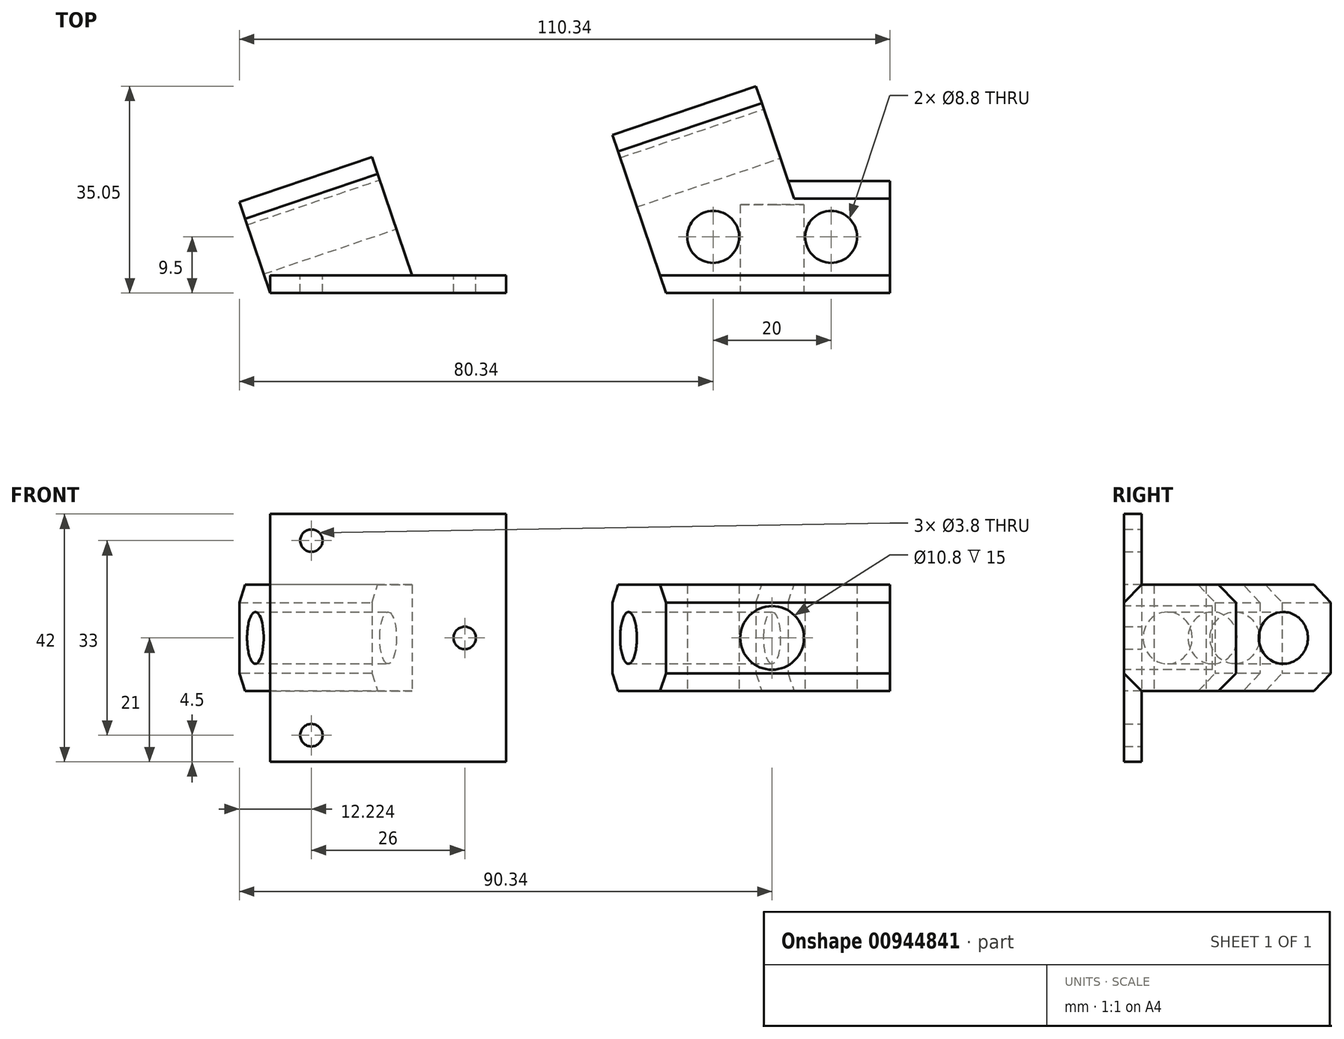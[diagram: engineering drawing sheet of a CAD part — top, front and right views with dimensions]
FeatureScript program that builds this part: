
annotation { "Feature Type Name" : "Feature", "Feature Type Description" : "" }
export const myFeature = defineFeature(function(context is Context, id is Id, definition is map)
    precondition{}
    {
        {
            var Q0;
            Q0=qCreatedBy(makeId("Top.planeOp"),FACE);
            var sketch = newSketch(context, id + "F0", { "sketchPlane" : qUnion([Q0])});
            skLineSegment(sketch, "E0.bottom", {"start": v(0, 0) * mm, "end": v(38, 0) * mm});
            skLineSegment(sketch, "E0.top", {"start": v(20.7, 19) * mm, "end": v(38, 19) * mm});
            skLineSegment(sketch, "E0.left", {"start": v(0, 0) * mm, "end": v(0, 19) * mm, "construction": true});
            skLineSegment(sketch, "E0.right", {"start": v(38, 0) * mm, "end": v(38, 19) * mm});
            skCircle(sketch, "E1", {"center": v(28, 9.5) * mm, "radius": 4.4 * mm});
            skPoint(sketch, "E1.centerSnap0", {"position": v(38, 9.5) * mm});
            skCircle(sketch, "E2", {"center": v(8, 9.5) * mm, "radius": 4.4 * mm});
            skLineSegment(sketch, "E3", {"start": v(8, 9.5) * mm, "end": v(28, 9.5) * mm, "construction": true});
            skLineSegment(sketch, "E4", {"start": v(18, 9.5) * mm, "end": v(18, 27) * mm, "construction": true});
            skLineSegment(sketch, "E5", {"start": v(18, 27) * mm, "end": v(-19.64, 14.26) * mm, "construction": true});
            skLineSegment(sketch, "E6", {"start": v(15.27, 35.05) * mm, "end": v(20.7, 19) * mm});
            skLineSegment(sketch, "E7", {"start": v(15.27, 35.05) * mm, "end": v(-9.07, 26.8) * mm});
            skLineSegment(sketch, "E8", {"start": v(0, 0) * mm, "end": v(-9.07, 26.8) * mm});
            skLineSegment(sketch, "E9", {"start": v(-67.12, 0) * mm, "end": v(-27.12, 0) * mm});
            skLineSegment(sketch, "E10", {"start": v(-27.12, 0) * mm, "end": v(-27.12, 3) * mm});
            skLineSegment(sketch, "E11", {"start": v(-27.12, 3) * mm, "end": v(-67.12, 3) * mm});
            skLineSegment(sketch, "E12", {"start": v(-67.12, 3) * mm, "end": v(-67.12, 0) * mm});
            skLineSegment(sketch, "E13", {"start": v(-47.12, 0) * mm, "end": v(-47.12, 15) * mm, "construction": true});
            skPoint(sketch, "E13.endSnap0", {"position": v(-47.12, 3) * mm});
            skLineSegment(sketch, "E14", {"start": v(-47.12, 15) * mm, "end": v(-73.5, 6.07) * mm, "construction": true});
            skLineSegment(sketch, "E15", {"start": v(-49.84, 23.05) * mm, "end": v(-43.05, 3) * mm});
            skLineSegment(sketch, "E16", {"start": v(-49.84, 23.05) * mm, "end": v(-72.34, 15.44) * mm});
            skLineSegment(sketch, "E17", {"start": v(-72.34, 15.44) * mm, "end": v(-67.12, 0) * mm});
            skSolve(sketch);
        }
        {
            var Q0;
            Q0=makeQuery(id+"F0.imprint","IMPRINT",FACE,{"disambiguationData":[TD([[makeQuery(id+"F0.imprint","IMPRINT",EDGE,{"derivedFrom":sQuery(id+"F0.wireOp",EDGE,"E0.bottom")}),1.0]])]});
            extrude(context, id + "F1", {"entities" : qUnion([Q0]), "depth" : 18 * mm, "offsetDistance" : 25 * mm});
        }
        {
            var Q0;
            Q0=qCreatedBy(makeId("Front.planeOp"),FACE);
            var sketch = newSketch(context, id + "F2", { "sketchPlane" : qUnion([Q0])});
            skCircle(sketch, "E18", {"center": v(18, 9) * mm, "radius": 5.4 * mm});
            skSolve(sketch);
        }
        {
            var Q0;
            Q0=makeQuery(id+"F2.imprint","IMPRINT",FACE,{"disambiguationData":[TD([[makeQuery(id+"F2.imprint","IMPRINT",EDGE,{"derivedFrom":sQuery(id+"F2.wireOp",EDGE,"E18")}),1.0]])]});
            extrude(context, id + "F3", {"entities" : qUnion([Q0]), "operationType" : NewBodyOperationType.REMOVE, "oppositeDirection" : true, "depth" : 15 * mm, "offsetDistance" : 25 * mm});
        }
        {
            var Q0;
            Q0=makeQuery(id+"F1.opExtrude","SWEPT_FACE",FACE,{"disambiguationData":[OSD([sQuery(id+"F0.wireOp",EDGE,"E6")])]});
            var sketch = newSketch(context, id + "F4", { "sketchPlane" : qUnion([Q0])});
            skCircle(sketch, "E19", {"center": v(19.8, 9) * mm, "radius": 4.4 * mm});
            skPoint(sketch, "E19.centerSnap0", {"position": v(28.3, 9) * mm});
            skSolve(sketch);
        }
        {
            var Q0;
            Q0=makeQuery(id+"F4.imprint","IMPRINT",FACE,{"disambiguationData":[TD([[makeQuery(id+"F4.imprint","IMPRINT",EDGE,{"derivedFrom":sQuery(id+"F4.wireOp",EDGE,"E19")}),1.0]])]});
            extrude(context, id + "F5", {"entities" : qUnion([Q0]), "operationType" : NewBodyOperationType.REMOVE, "oppositeDirection" : true, "depth" : 55 * mm, "offsetDistance" : 25 * mm});
        }
        {
            var Q0;
            Q0=makeQuery(id+"F1.opExtrude","CAP_EDGE",EDGE,{"disambiguationData":[OSD([sQuery(id+"F0.wireOp",EDGE,"E7")])],"isStart":false});
            var Q1;
            Q1=makeQuery(id+"F1.opExtrude","CAP_EDGE",EDGE,{"disambiguationData":[OSD([sQuery(id+"F0.wireOp",EDGE,"E7")])],"isStart":true});
            var Q2;
            Q2=makeQuery(id+"F1.opExtrude","CAP_EDGE",EDGE,{"disambiguationData":[OSD([sQuery(id+"F0.wireOp",EDGE,"E0.top")])],"isStart":false});
            var Q3;
            Q3=makeQuery(id+"F1.opExtrude","CAP_EDGE",EDGE,{"disambiguationData":[OSD([sQuery(id+"F0.wireOp",EDGE,"E0.top")])],"isStart":true});
            var Q4;
            Q4=makeQuery(id+"F1.opExtrude","CAP_EDGE",EDGE,{"disambiguationData":[OSD([sQuery(id+"F0.wireOp",EDGE,"E0.bottom")])],"isStart":false});
            var Q5;
            Q5=makeQuery(id+"F1.opExtrude","CAP_EDGE",EDGE,{"disambiguationData":[OSD([sQuery(id+"F0.wireOp",EDGE,"E0.bottom")])],"isStart":true});
            chamfer(context, id + "F6", {"entities" : qUnion([Q0, Q1, Q2, Q3, Q4, Q5]), "width" : 3 * mm, "tangentPropagation" : true});
        }
        {
            var Q0;
            {var subQ1=sQuery(id+"F0.wireOp",EDGE,"E12");Q0=makeQuery(id+"F0.imprint","IMPRINT",FACE,{"disambiguationData":[TD([[makeQuery(id+"F0.imprint","IMPRINT",EDGE,{"derivedFrom":subQ1}),-1.0]])]});}
            extrude(context, id + "F7", {"entities" : qUnion([Q0]), "depth" : 18 * mm, "offsetDistance" : 25 * mm});
        }
        {
            var Q0;
            Q0=makeQuery(id+"F0.imprint","IMPRINT",FACE,{"disambiguationData":[TD([[makeQuery(id+"F0.imprint","IMPRINT",EDGE,{"derivedFrom":sQuery(id+"F0.wireOp",EDGE,"E9")}),1.0]])]});
            extrude(context, id + "F8", {"entities" : qUnion([Q0]), "operationType" : NewBodyOperationType.ADD, "depth" : 30 * mm, "offsetDistance" : 25 * mm, "hasSecondDirection" : true, "secondDirectionOppositeDirection" : true, "secondDirectionDepth" : 12 * mm});
        }
        {
            var Q0;
            Q0=makeQuery(id+"F7.opExtrude","SWEPT_FACE",FACE,{"disambiguationData":[OSD([sQuery(id+"F0.wireOp",EDGE,"E15")])]});
            var sketch = newSketch(context, id + "F9", { "sketchPlane" : qUnion([Q0])});
            skCircle(sketch, "E20", {"center": v(29.31, 9) * mm, "radius": 4.4 * mm});
            skPoint(sketch, "E21", {"position": v(37.81, 9) * mm});
            skSolve(sketch);
        }
        {
            var Q0;
            Q0=makeQuery(id+"F9.imprint","IMPRINT",FACE,{"disambiguationData":[TD([[makeQuery(id+"F9.imprint","IMPRINT",EDGE,{"derivedFrom":sQuery(id+"F9.wireOp",EDGE,"E20")}),1.0]])]});
            extrude(context, id + "F10", {"entities" : qUnion([Q0]), "operationType" : NewBodyOperationType.REMOVE, "oppositeDirection" : true, "depth" : 45 * mm, "offsetDistance" : 25 * mm});
        }
        {
            var Q0;
            Q0=makeQuery(id+"F7.opExtrude","CAP_EDGE",EDGE,{"disambiguationData":[OSD([sQuery(id+"F0.wireOp",EDGE,"E16")])],"isStart":false});
            var Q1;
            Q1=makeQuery(id+"F7.opExtrude","CAP_EDGE",EDGE,{"disambiguationData":[OSD([sQuery(id+"F0.wireOp",EDGE,"E16")])],"isStart":true});
            var Q2;
            Q2=makeQuery(id+"F7.opExtrude","CAP_EDGE",EDGE,{"disambiguationData":[OSD([sQuery(id+"F0.wireOp",EDGE,"E11")])],"isStart":false});
            var Q3;
            Q3=makeQuery(id+"F7.opExtrude","CAP_EDGE",EDGE,{"disambiguationData":[OSD([sQuery(id+"F0.wireOp",EDGE,"E11")])],"isStart":true});
            chamfer(context, id + "F11", {"entities" : qUnion([Q0, Q1, Q2, Q3]), "width" : 3 * mm, "tangentPropagation" : true});
        }
        {
            var Q0;
            Q0=makeQuery(id+"F8.opExtrude","SWEPT_FACE",FACE,{"disambiguationData":[OSD([sQuery(id+"F0.wireOp",EDGE,"E11")])]});
            var sketch = newSketch(context, id + "F12", { "sketchPlane" : qUnion([Q0])});
            skCircle(sketch, "E22", {"center": v(34.12, 9) * mm, "radius": 1.9 * mm});
            skCircle(sketch, "E23", {"center": v(60.12, 25.5) * mm, "radius": 1.9 * mm});
            skPoint(sketch, "E24", {"position": v(27.12, 9) * mm});
            skCircle(sketch, "E25", {"center": v(60.12, -7.5) * mm, "radius": 1.9 * mm});
            skSolve(sketch);
        }
        {
            var Q0;
            Q0=makeQuery(id+"F12.imprint","IMPRINT",FACE,{"disambiguationData":[TD([[makeQuery(id+"F12.imprint","IMPRINT",EDGE,{"derivedFrom":sQuery(id+"F12.wireOp",EDGE,"E25")}),1.0]])]});
            var Q1;
            Q1=makeQuery(id+"F12.imprint","IMPRINT",FACE,{"disambiguationData":[TD([[makeQuery(id+"F12.imprint","IMPRINT",EDGE,{"derivedFrom":sQuery(id+"F12.wireOp",EDGE,"E23")}),1.0]])]});
            var Q2;
            Q2=makeQuery(id+"F12.imprint","IMPRINT",FACE,{"disambiguationData":[TD([[makeQuery(id+"F12.imprint","IMPRINT",EDGE,{"derivedFrom":sQuery(id+"F12.wireOp",EDGE,"E22")}),1.0]])]});
            extrude(context, id + "F13", {"entities" : qUnion([Q0, Q1, Q2]), "operationType" : NewBodyOperationType.REMOVE, "oppositeDirection" : true, "depth" : 25 * mm, "offsetDistance" : 25 * mm});
        }
    });
